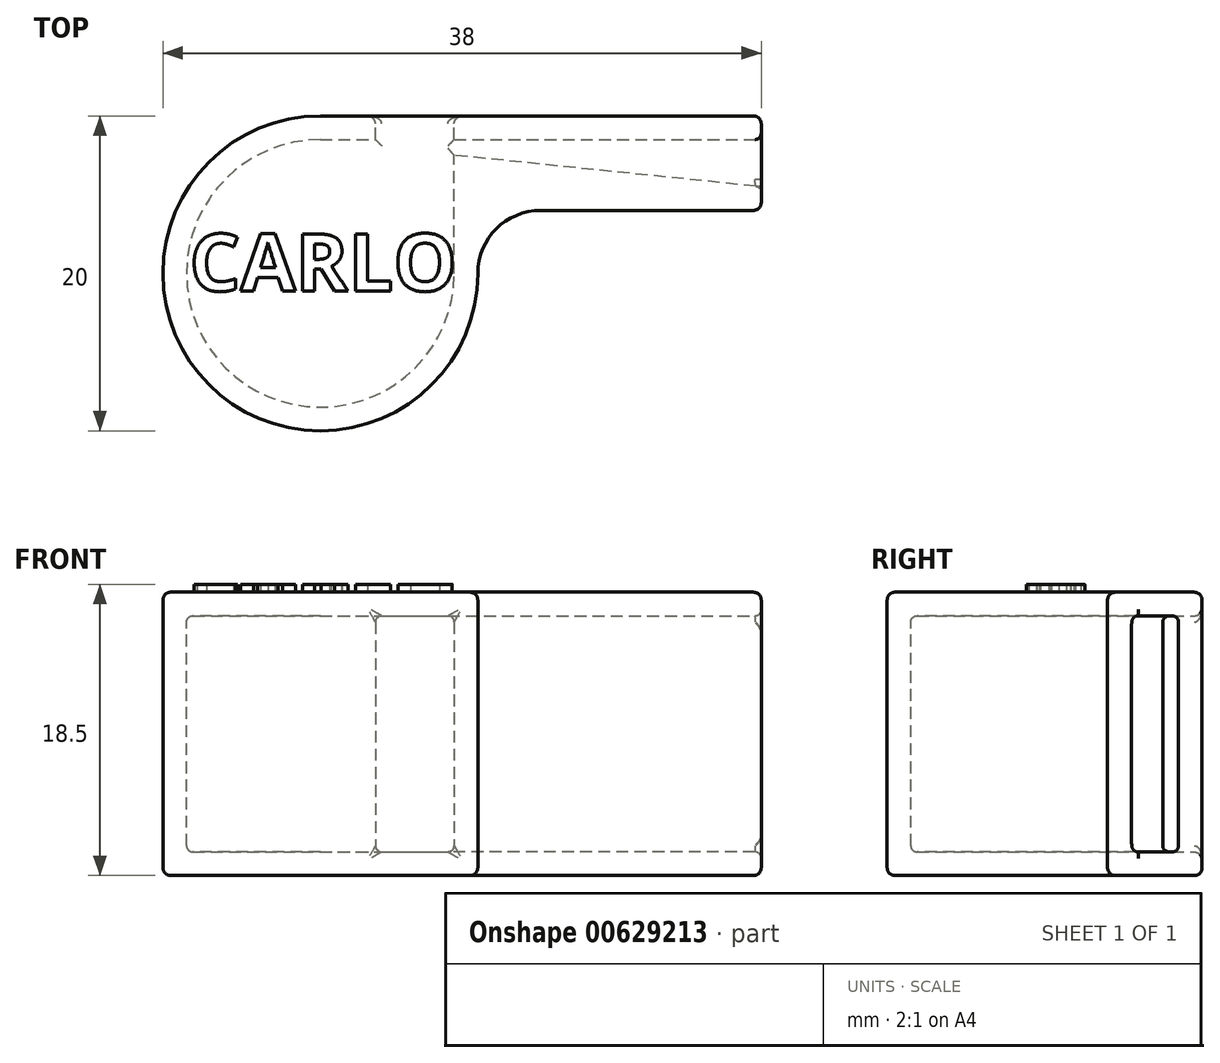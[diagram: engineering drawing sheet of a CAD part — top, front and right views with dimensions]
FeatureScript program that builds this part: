
annotation { "Feature Type Name" : "Feature", "Feature Type Description" : "" }
export const myFeature = defineFeature(function(context is Context, id is Id, definition is map)
    precondition{}
    {
        {
            var Q0;
            Q0=qCreatedBy(makeId("Top.planeOp"),FACE);
            var sketch = newSketch(context, id + "F0", { "sketchPlane" : qUnion([Q0])});
            skArc(sketch, "E0", {"start": v(0, 10) * mm, "mid": v(-7.07, -7.07) * mm, "end": v(10, 0) * mm});
            skLineSegment(sketch, "E1", {"start": v(0, 10) * mm, "end": v(28, 10) * mm});
            skLineSegment(sketch, "E2", {"start": v(28, 10) * mm, "end": v(28, 4) * mm});
            skLineSegment(sketch, "E3", {"start": v(28, 4) * mm, "end": v(10, 4) * mm});
            skArc(sketch, "E4", {"start": v(0, 8.5) * mm, "mid": v(-6.01, -6.01) * mm, "end": v(8.5, 0) * mm});
            skLineSegment(sketch, "E5", {"start": v(0, 8.5) * mm, "end": v(28, 8.5) * mm});
            skLineSegment(sketch, "E6", {"start": v(28, 5.5) * mm, "end": v(8.5, 7.5) * mm});
            skLineSegment(sketch, "E7", {"start": v(10, 0) * mm, "end": v(10, 4) * mm});
            skLineSegment(sketch, "E8", {"start": v(8.5, 0) * mm, "end": v(8.5, 7.5) * mm});
            skSolve(sketch);
        }
        {
            var Q0;
            Q0=makeQuery(id+"F0.imprint","IMPRINT",FACE,{"disambiguationData":[TD([[makeQuery(id+"F0.imprint","IMPRINT",EDGE,{"derivedFrom":sQuery(id+"F0.wireOp",EDGE,"E0")}),1.0]])]});
            var Q1;
            Q1=makeQuery(id+"F0.imprint","IMPRINT",FACE,{"disambiguationData":[TD([[makeQuery(id+"F0.imprint","IMPRINT",EDGE,{"derivedFrom":sQuery(id+"F0.wireOp",EDGE,"E4")}),1.0]])]});
            extrude(context, id + "F1", {"entities" : qUnion([Q0, Q1]), "endBound" : BoundingType.SYMMETRIC, "depth" : 18 * mm});
        }
        {
            var Q0;
            Q0=makeQuery(id+"F0.imprint","IMPRINT",FACE,{"disambiguationData":[TD([[makeQuery(id+"F0.imprint","IMPRINT",EDGE,{"derivedFrom":sQuery(id+"F0.wireOp",EDGE,"E4")}),1.0]])]});
            extrude(context, id + "F2", {"entities" : qUnion([Q0]), "operationType" : NewBodyOperationType.REMOVE, "endBound" : BoundingType.SYMMETRIC, "oppositeDirection" : true, "depth" : 15 * mm});
        }
        {
            var Q0;
            Q0=makeQuery(id+"F1.opExtrude","SWEPT_FACE",FACE,{"disambiguationData":[OSD([sQuery(id+"F0.wireOp",EDGE,"E1")])]});
            var sketch = newSketch(context, id + "F3", { "sketchPlane" : qUnion([Q0])});
            skLineSegment(sketch, "E9.bottom", {"start": v(-3.5, 7.5) * mm, "end": v(-8.5, 7.5) * mm});
            skLineSegment(sketch, "E9.top", {"start": v(-3.5, -7.5) * mm, "end": v(-8.5, -7.5) * mm});
            skLineSegment(sketch, "E9.left", {"start": v(-3.5, 7.5) * mm, "end": v(-3.5, -7.5) * mm});
            skLineSegment(sketch, "E9.right", {"start": v(-8.5, 7.5) * mm, "end": v(-8.5, -7.5) * mm});
            skSolve(sketch);
        }
        {
            var Q0;
            Q0=makeQuery(id+"F3.imprint","IMPRINT",FACE,{"disambiguationData":[TD([[makeQuery(id+"F3.imprint","IMPRINT",EDGE,{"derivedFrom":sQuery(id+"F3.wireOp",EDGE,"E9.bottom")}),1.0]])]});
            extrude(context, id + "F4", {"entities" : qUnion([Q0]), "operationType" : NewBodyOperationType.REMOVE, "endBound" : BoundingType.UP_TO_NEXT, "oppositeDirection" : true, "depth" : 25 * mm});
        }
        {
            var Q0;
            Q0=makeQuery(id+"F1.opExtrude","SWEPT_EDGE",EDGE,{"disambiguationData":[OSD([sQuery(id+"F0.wireOp",EDGE,"E3"),sQuery(id+"F0.wireOp",EDGE,"E7")])]});
            fillet(context, id + "F5", {"entities" : qUnion([Q0]), "radius" : 4 * mm, "tangentPropagation" : true, "allowEdgeOverflow" : false});
        }
        {
            var Q0;
            Q0=makeQuery(id+"F1.opExtrude","CAP_FACE",FACE,{"disambiguationData":[OSD([sQuery(id+"F0.wireOp",EDGE,"E0"),sQuery(id+"F0.wireOp",EDGE,"E1"),sQuery(id+"F0.wireOp",EDGE,"E2"),sQuery(id+"F0.wireOp",EDGE,"E3"),sQuery(id+"F0.wireOp",EDGE,"E7")])],"isStart":true});
            var Q1;
            Q1=makeQuery(id+"F1.opExtrude","CAP_FACE",FACE,{"disambiguationData":[OSD([sQuery(id+"F0.wireOp",EDGE,"E0"),sQuery(id+"F0.wireOp",EDGE,"E1"),sQuery(id+"F0.wireOp",EDGE,"E2"),sQuery(id+"F0.wireOp",EDGE,"E3"),sQuery(id+"F0.wireOp",EDGE,"E7")])],"isStart":false});
            var Q2;
            Q2=makeQuery(id+"F1.opExtrude","SWEPT_FACE",FACE,{"disambiguationData":[OSD([sQuery(id+"F0.wireOp",EDGE,"E1")])]});
            var Q3;
            Q3=makeQuery(id+"FfO7nH7XfML7F3A_1.opExtrude","SWEPT_FACE",FACE,{"disambiguationData":[OSD([sQuery(id+"FNt9KbUhkB5fkIH_1.wireOp",EDGE,"Q0lx9wTe-g1rZ-dtUQ-Mbc8-OocmhmDDGcm9")])]});
            var Q4;
            Q4=makeQuery(id+"F1.opExtrude","SWEPT_EDGE",EDGE,{"disambiguationData":[OSD([sQuery(id+"F0.wireOp",EDGE,"E2"),sQuery(id+"F0.wireOp",EDGE,"E3")])]});
            fillet(context, id + "F6", {"entities" : qUnion([Q0, Q1, Q2, Q3, Q4]), "radius" : 0.5 * mm, "tangentPropagation" : true, "allowEdgeOverflow" : false});
        }
        {
            var Q0;
            Q0=makeQuery(id+"F2.boolean.opBoolean","COPY",EDGE,{"derivedFrom":makeQuery(id+"F2.opExtrude","CAP_EDGE",EDGE,{"disambiguationData":[OSD([sQuery(id+"F0.wireOp",EDGE,"E6")])],"isStart":true})});
            var Q1;
            {var subQ0=sQuery(id+"F0.wireOp",EDGE,"E5");var subQ1=sQuery(id+"F0.wireOp",EDGE,"E2");Q1=makeQuery(id+"F4.boolean.opBoolean","SPLIT",EDGE,{"disambiguationData":[TD([makeQuery(id+"F1.opExtrude","SWEPT_FACE",FACE,{"disambiguationData":[OSD([subQ1])]})])],"derivedFrom":makeQuery(id+"F2.boolean.opBoolean","COPY",EDGE,{"derivedFrom":makeQuery(id+"F2.opExtrude","CAP_EDGE",EDGE,{"disambiguationData":[OSD([subQ0])],"isStart":true})})});}
            var Q2;
            {var subQ0=sQuery(id+"F0.wireOp",EDGE,"E5");var subQ1=sQuery(id+"F0.wireOp",EDGE,"E2");Q2=makeQuery(id+"F4.boolean.opBoolean","SPLIT",EDGE,{"disambiguationData":[TD([makeQuery(id+"F1.opExtrude","SWEPT_FACE",FACE,{"disambiguationData":[OSD([subQ1])]})])],"derivedFrom":makeQuery(id+"F2.boolean.opBoolean","COPY",EDGE,{"derivedFrom":makeQuery(id+"F2.opExtrude","CAP_EDGE",EDGE,{"disambiguationData":[OSD([subQ0])],"isStart":false})})});}
            var Q3;
            Q3=makeQuery(id+"F2.boolean.opBoolean","COPY",EDGE,{"derivedFrom":makeQuery(id+"F2.opExtrude","CAP_EDGE",EDGE,{"disambiguationData":[OSD([sQuery(id+"F0.wireOp",EDGE,"E6")])],"isStart":false})});
            var Q4;
            Q4=makeQuery(id+"F2.boolean.opBoolean","COPY",EDGE,{"derivedFrom":makeQuery(id+"F2.opExtrude","CAP_EDGE",EDGE,{"disambiguationData":[OSD([sQuery(id+"F0.wireOp",EDGE,"E2")])],"isStart":true})});
            var Q5;
            Q5=makeQuery(id+"F2.boolean.opBoolean","COPY",EDGE,{"derivedFrom":makeQuery(id+"F2.opExtrude","SWEPT_EDGE",EDGE,{"disambiguationData":[OSD([sQuery(id+"F0.wireOp",EDGE,"E2"),sQuery(id+"F0.wireOp",EDGE,"E6")])]})});
            var Q6;
            Q6=makeQuery(id+"F4.boolean.opBoolean","MERGE",FACE,{"derivedFrom":[makeQuery(id+"F2.boolean.opBoolean","COPY",FACE,{"derivedFrom":makeQuery(id+"F2.opExtrude","CAP_FACE",FACE,{"disambiguationData":[OSD([sQuery(id+"F0.wireOp",EDGE,"E2"),sQuery(id+"F0.wireOp",EDGE,"E4"),sQuery(id+"F0.wireOp",EDGE,"E5"),sQuery(id+"F0.wireOp",EDGE,"E6"),sQuery(id+"F0.wireOp",EDGE,"E8")])],"isStart":false})}),makeQuery(id+"F4.opExtrude","SWEPT_FACE",FACE,{"disambiguationData":[OSD([sQuery(id+"F3.wireOp",EDGE,"E9.top")])]})]});
            var Q7;
            Q7=makeQuery(id+"F4.boolean.opBoolean","MERGE",FACE,{"derivedFrom":[makeQuery(id+"F2.boolean.opBoolean","COPY",FACE,{"derivedFrom":makeQuery(id+"F2.opExtrude","CAP_FACE",FACE,{"disambiguationData":[OSD([sQuery(id+"F0.wireOp",EDGE,"E2"),sQuery(id+"F0.wireOp",EDGE,"E4"),sQuery(id+"F0.wireOp",EDGE,"E5"),sQuery(id+"F0.wireOp",EDGE,"E6"),sQuery(id+"F0.wireOp",EDGE,"E8")])],"isStart":true})}),makeQuery(id+"F4.opExtrude","SWEPT_FACE",FACE,{"disambiguationData":[OSD([sQuery(id+"F3.wireOp",EDGE,"E9.bottom")])]})]});
            fillet(context, id + "F7", {"entities" : qUnion([Q0, Q1, Q2, Q3, Q4, Q5, Q6, Q7]), "radius" : 0.4 * mm, "tangentPropagation" : true, "allowEdgeOverflow" : false});
        }
        {
            var Q0;
            Q0=makeQuery(id+"F1.opExtrude","CAP_FACE",FACE,{"disambiguationData":[OSD([sQuery(id+"F0.wireOp",EDGE,"E0"),sQuery(id+"F0.wireOp",EDGE,"E1"),sQuery(id+"F0.wireOp",EDGE,"E2"),sQuery(id+"F0.wireOp",EDGE,"E3"),sQuery(id+"F0.wireOp",EDGE,"E7")])],"isStart":false});
            var sketch = newSketch(context, id + "F8", { "sketchPlane" : qUnion([Q0])});
            skText(sketch, "E10", { "text": "CARLO", "fontName": "OpenSans-Bold.ttf"});
            const initialGuessF8  = {"E10": [-0.00831, -0.00112, 1, 0, 0.00365]};
            skSetInitialGuess(sketch, initialGuessF8);
            skSolve(sketch);
        }
        {
            var Q0;
            Q0 = qSketchRegion(id + "F8", true);
            extrude(context, id + "F9", {"entities" : qUnion([Q0]), "operationType" : NewBodyOperationType.ADD, "depth" : 0.5 * mm, "offsetDistance" : 25 * mm});
        }
    });
